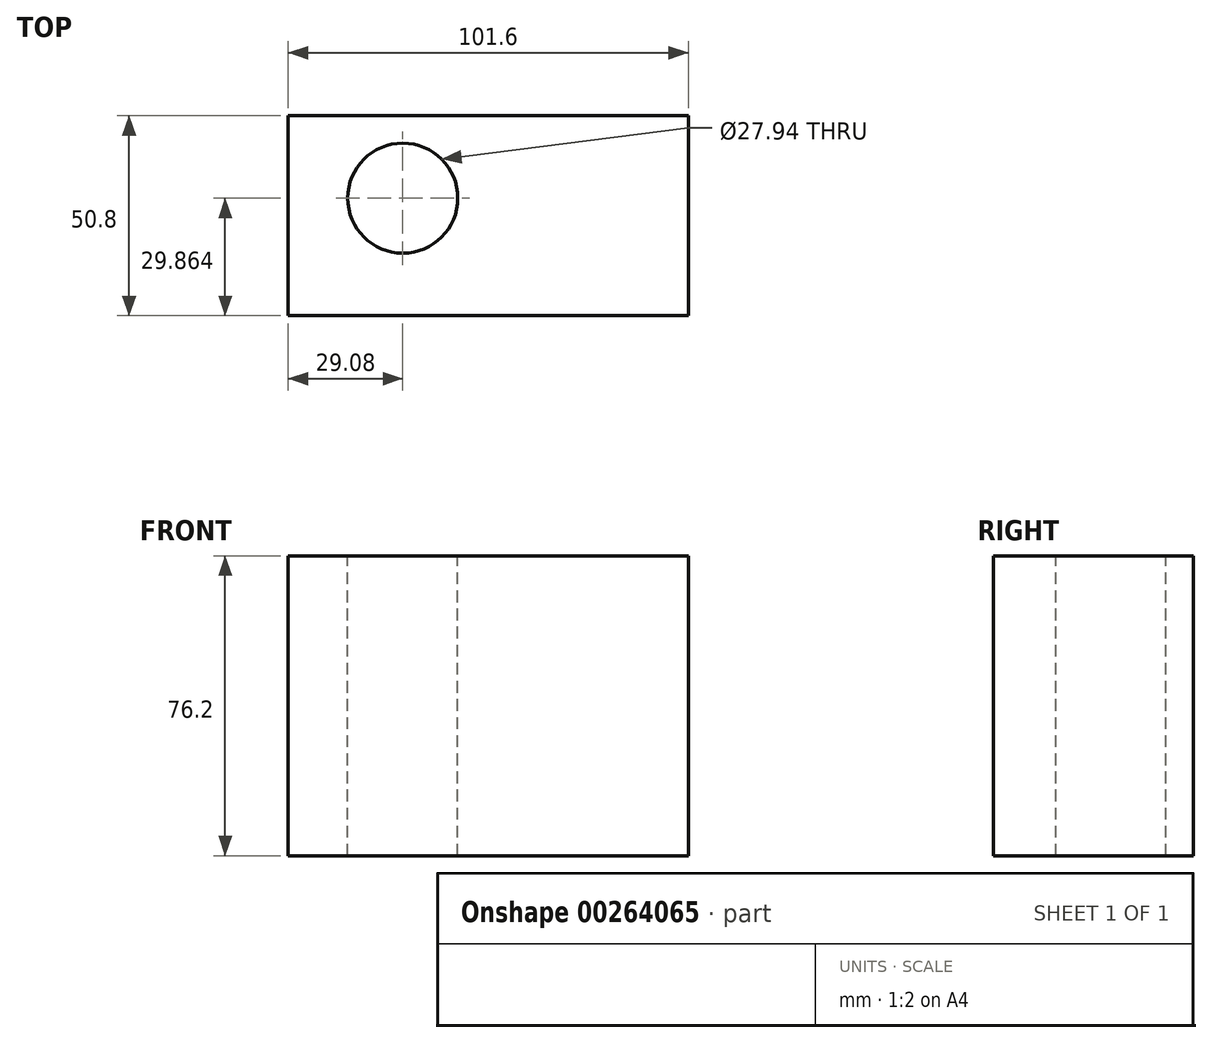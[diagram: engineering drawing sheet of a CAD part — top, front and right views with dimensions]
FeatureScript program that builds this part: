
annotation { "Feature Type Name" : "Feature", "Feature Type Description" : "" }
export const myFeature = defineFeature(function(context is Context, id is Id, definition is map)
    precondition{}
    {
        {
            var Q0;
            Q0=qCreatedBy(makeId("Front.planeOp"),FACE);
            var sketch = newSketch(context, id + "F0", { "sketchPlane" : qUnion([Q0])});
            skLineSegment(sketch, "E0.bottom", {"start": v(0, 0) * mm, "end": v(101.6, 0) * mm});
            skLineSegment(sketch, "E0.top", {"start": v(0, 76.2) * mm, "end": v(101.6, 76.2) * mm});
            skLineSegment(sketch, "E0.left", {"start": v(0, 0) * mm, "end": v(0, 76.2) * mm});
            skLineSegment(sketch, "E0.right", {"start": v(101.6, 0) * mm, "end": v(101.6, 76.2) * mm});
            skSolve(sketch);
        }
        {
            var Q0;
            Q0=makeQuery(id+"F0.imprint","IMPRINT",FACE,{"disambiguationData":[TD([[makeQuery(id+"F0.imprint","IMPRINT",EDGE,{"derivedFrom":sQuery(id+"F0.wireOp",EDGE,"E0.bottom")}),1.0]])]});
            extrude(context, id + "F1", {"entities" : qUnion([Q0]), "depth" : 50.8 * mm});
        }
        {
            var Q0;
            Q0=makeQuery(id+"F1.opExtrude","SWEPT_FACE",FACE,{"disambiguationData":[OSD([sQuery(id+"F0.wireOp",EDGE,"E0.top")])]});
            var sketch = newSketch(context, id + "F2", { "sketchPlane" : qUnion([Q0])});
            skCircle(sketch, "E1", {"center": v(29.08, -20.94) * mm, "radius": 13.97 * mm});
            skSolve(sketch);
        }
        {
            var Q0;
            Q0 = qSketchRegion(id + "F2", true);
            extrude(context, id + "F3", {"entities" : qUnion([Q0]), "operationType" : NewBodyOperationType.REMOVE, "endBound" : BoundingType.UP_TO_NEXT, "oppositeDirection" : true, "depth" : 25.4 * mm});
        }
    });
